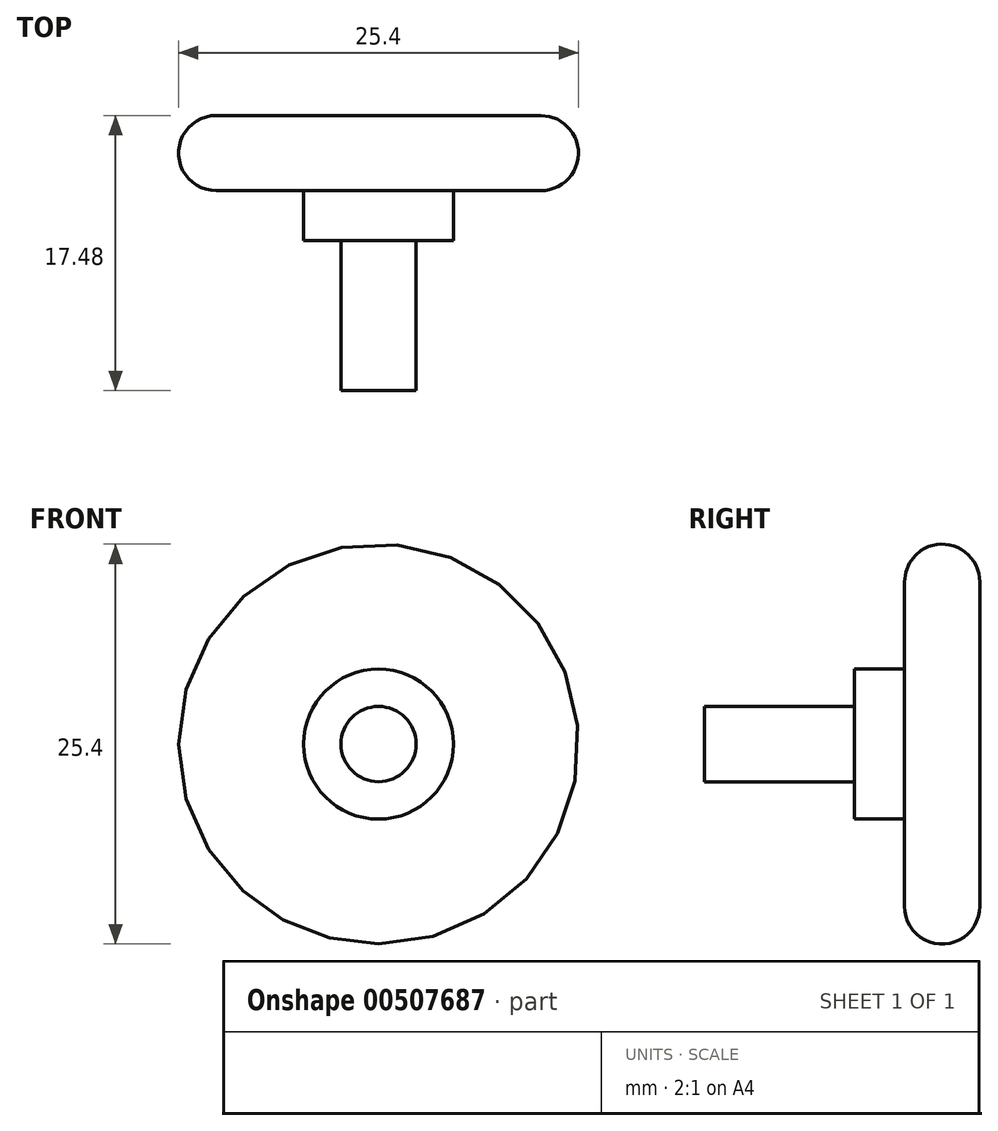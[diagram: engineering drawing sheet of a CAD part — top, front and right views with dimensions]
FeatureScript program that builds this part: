
annotation { "Feature Type Name" : "Feature", "Feature Type Description" : "" }
export const myFeature = defineFeature(function(context is Context, id is Id, definition is map)
    precondition{}
    {
        {
            var Q0;
            Q0=qCreatedBy(makeId("Front.planeOp"),FACE);
            var sketch = newSketch(context, id + "F0", { "sketchPlane" : qUnion([Q0])});
            skCircle(sketch, "E0", {"center": v(0, 0) * mm, "radius": 12.7 * mm});
            skSolve(sketch);
        }
        {
            var Q0;
            Q0 = qSketchRegion(id + "F0", true);
            extrude(context, id + "F1", {"entities" : qUnion([Q0]), "depth" : 4.78 * mm, "offsetDistance" : 25.4 * mm});
        }
        {
            var Q0;
            Q0=makeQuery(id+"F1.opExtrude","CAP_EDGE",EDGE,{"disambiguationData":[OSD([sQuery(id+"F0.wireOp",EDGE,"E0")])],"isStart":false});
            var Q1;
            Q1=makeQuery(id+"F1.opExtrude","CAP_EDGE",EDGE,{"disambiguationData":[OSD([sQuery(id+"F0.wireOp",EDGE,"E0")])],"isStart":true});
            fillet(context, id + "F2", {"entities" : qUnion([Q0, Q1]), "radius" : 2.4 * mm, "tangentPropagation" : true, "allowEdgeOverflow" : false});
        }
        {
            var Q0;
            Q0=makeQuery(id+"F1.opExtrude","CAP_FACE",FACE,{"disambiguationData":[OSD([sQuery(id+"F0.wireOp",EDGE,"E0")])],"isStart":false});
            var sketch = newSketch(context, id + "F3", { "sketchPlane" : qUnion([Q0])});
            skCircle(sketch, "E1.0.0", {"center": v(0, 0) * mm, "radius": 10.31 * mm});
            skCircle(sketch, "E2", {"center": v(0, 0) * mm, "radius": 4.76 * mm});
            skSolve(sketch);
        }
        {
            var Q0;
            Q0=makeQuery(id+"F3.imprint","IMPRINT",FACE,{"disambiguationData":[TD([[makeQuery(id+"F3.imprint","IMPRINT",EDGE,{"derivedFrom":sQuery(id+"F3.wireOp",EDGE,"E2")}),1.0]])]});
            extrude(context, id + "F4", {"entities" : qUnion([Q0]), "operationType" : NewBodyOperationType.ADD, "depth" : 3.17 * mm});
        }
        {
            var Q0;
            Q0=makeQuery(id+"F4.opExtrude","CAP_FACE",FACE,{"disambiguationData":[OSD([sQuery(id+"F3.wireOp",EDGE,"E2")])],"isStart":false});
            var sketch = newSketch(context, id + "F5", { "sketchPlane" : qUnion([Q0])});
            skCircle(sketch, "E3.0", {"center": v(0, 0) * mm, "radius": 4.76 * mm});
            skCircle(sketch, "E4", {"center": v(0, 0) * mm, "radius": 2.39 * mm});
            skSolve(sketch);
        }
        {
            var Q0;
            Q0=makeQuery(id+"F5.imprint","IMPRINT",FACE,{"disambiguationData":[TD([[makeQuery(id+"F5.imprint","IMPRINT",EDGE,{"derivedFrom":sQuery(id+"F5.wireOp",EDGE,"E4")}),1.0]])]});
            extrude(context, id + "F6", {"entities" : qUnion([Q0]), "operationType" : NewBodyOperationType.ADD, "depth" : 9.52 * mm});
        }
    });
